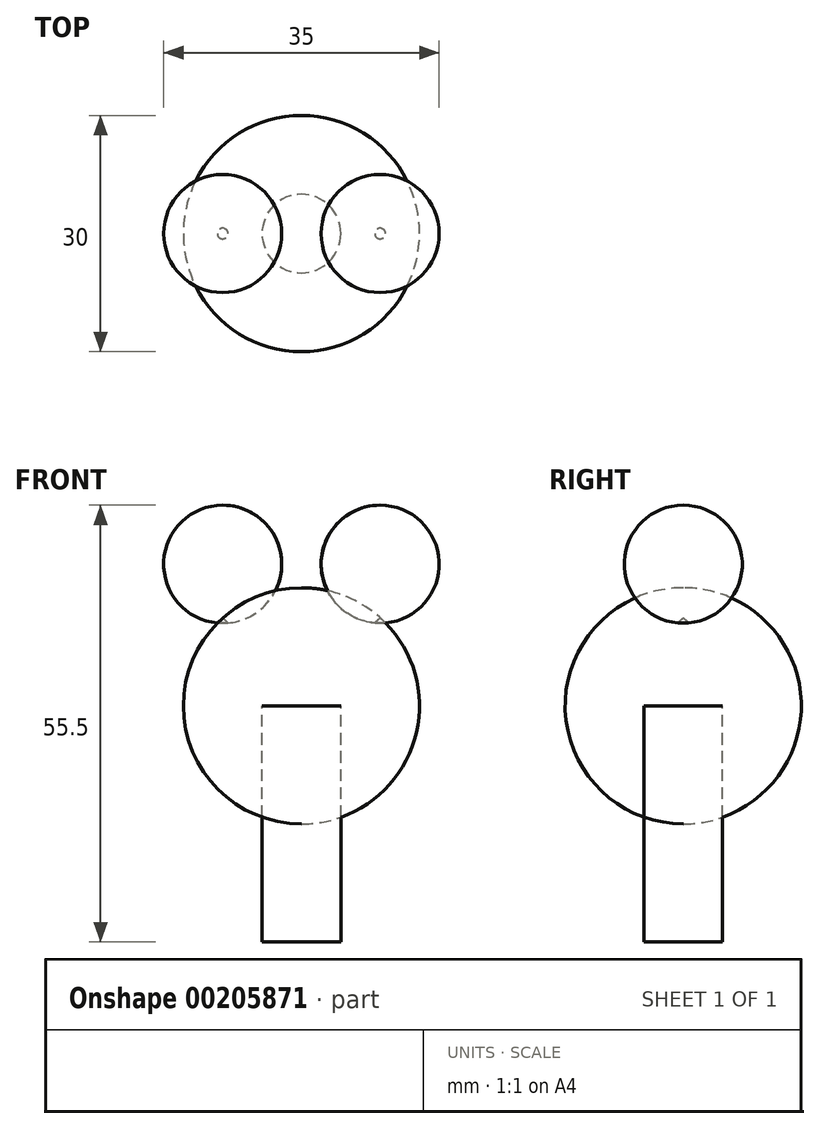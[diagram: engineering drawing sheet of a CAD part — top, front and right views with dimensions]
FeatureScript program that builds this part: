
annotation { "Feature Type Name" : "Feature", "Feature Type Description" : "" }
export const myFeature = defineFeature(function(context is Context, id is Id, definition is map)
    precondition{}
    {
        {
            var Q0;
            Q0=qCreatedBy(makeId("Front.planeOp"),FACE);
            var sketch = newSketch(context, id + "F0", { "sketchPlane" : qUnion([Q0])});
            skArc(sketch, "E0", {"start": v(0, 15) * mm, "mid": v(-15, 0) * mm, "end": v(0, -15) * mm});
            skArc(sketch, "E1", {"start": v(-10, 25.5) * mm, "mid": v(-17.5, 18) * mm, "end": v(-10, 10.5) * mm});
            skLineSegment(sketch, "E2", {"start": v(0, 49.4) * mm, "end": v(0, -36.14) * mm, "construction": true});
            skLineSegment(sketch, "E3", {"start": v(-10, 18) * mm, "end": v(-10, 43.94) * mm, "construction": true});
            skLineSegment(sketch, "E4", {"start": v(0, 15) * mm, "end": v(0, -15) * mm});
            skLineSegment(sketch, "E5", {"start": v(-10, 25.5) * mm, "end": v(-10, 10.5) * mm});
            skSolve(sketch);
        }
        {
            var Q0;
            {var subQ0=sQuery(id+"F0.wireOp",EDGE,"E4");Q0=makeQuery(id+"F0.imprint","IMPRINT",FACE,{"disambiguationData":[TD([[makeQuery(id+"F0.imprint","IMPRINT",EDGE,{"derivedFrom":subQ0}),-1.0]])]});}
            var Q1;
            {var subQ0=sQuery(id+"F0.wireOp",EDGE,"E5");var subQ1=sQuery(id+"F0.wireOp",EDGE,"E0");var subQ2=makeQuery(id+"F0.imprint","INTERSECT",VERTEX,{"derivedFrom":[subQ1,subQ0]});Q1=makeQuery(id+"F0.imprint","IMPRINT",FACE,{"disambiguationData":[TD([[makeQuery(id+"F0.imprint","IMPRINT",EDGE,{"disambiguationData":[TD([[subQ2,-1.0]])],"derivedFrom":subQ1}),1.0]])]});}
            var Q2;
            Q2=sQuery(id+"F0.wireOp",EDGE,"E2");
            revolve(context, id + "F1", {"entities" : qUnion([Q0, Q1]), "axis" : qUnion([Q2]), "revolveType" : RevolveType.FULL});
        }
        {
            var Q0;
            {var subQ0=sQuery(id+"F0.wireOp",EDGE,"E5");var subQ1=sQuery(id+"F0.wireOp",EDGE,"E0");var subQ2=makeQuery(id+"F0.imprint","INTERSECT",VERTEX,{"derivedFrom":[subQ1,subQ0]});Q0=makeQuery(id+"F0.imprint","IMPRINT",FACE,{"disambiguationData":[TD([[makeQuery(id+"F0.imprint","IMPRINT",EDGE,{"disambiguationData":[TD([[subQ2,-1.0]])],"derivedFrom":subQ1}),-1.0]])]});}
            var Q1;
            Q1=sQuery(id+"F0.wireOp",EDGE,"E5");
            revolve(context, id + "F2", {"entities" : qUnion([Q0]), "axis" : qUnion([Q1]), "revolveType" : RevolveType.FULL});
        }
        {
            var Q0;
            Q0=makeQuery(id+"F2.opRevolve","SWEPT_BODY",BODY,{"disambiguationData":[OSD([sQuery(id+"F0.wireOp",EDGE,"E0"),sQuery(id+"F0.wireOp",EDGE,"E1"),sQuery(id+"F0.wireOp",EDGE,"E5")])]});
            var Q1;
            Q1=qCreatedBy(makeId("Right.planeOp"),FACE);
            mirror(context, id + "F3", {"entities" : qUnion([Q0]), "mirrorPlane" : qUnion([Q1])});
        }
        {
            var Q0;
            Q0=qCreatedBy(makeId("Top.planeOp"),FACE);
            var sketch = newSketch(context, id + "F4", { "sketchPlane" : qUnion([Q0])});
            skCircle(sketch, "E6", {"center": v(0, 0) * mm, "radius": 5 * mm});
            skSolve(sketch);
        }
        {
            var Q0;
            Q0=qSketchRegion(id+"F4",true);
            extrude(context, id + "F5", {"entities" : qUnion([Q0]), "oppositeDirection" : true, "depth" : 30 * mm});
        }
    });
